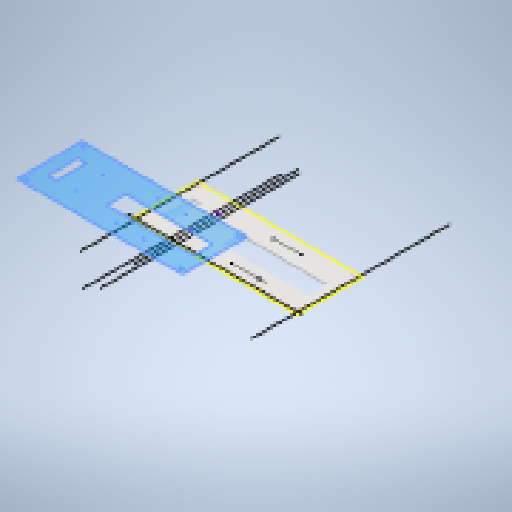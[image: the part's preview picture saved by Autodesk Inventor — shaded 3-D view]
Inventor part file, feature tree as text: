
AUTODESK INVENTOR PART (.ipt)
format: ipt  version: 2024 (Build 280153000, 153)  size: 231,424 bytes
history: native  units: mm
features: extrude x4, sketch x4, other x1
ambient origin geometry x8: Origin, YZ Plane, XZ Plane, XY Plane, X Axis, Y Axis, Z Axis, Center Point
bodies: Body1 (feature_tree)
feature tree (9):
  other  "솔리드1"
  extrude  "돌출1"  Depth=390.0mm
  sketch  "스케치2"
  extrude  "돌출2"  Depth=153.0mm
  extrude  "돌출3"  Depth=3.0mm TaperAngle=0.0deg
  extrude  "돌출5"  Depth=94.0mm
  sketch  "스케치1"
  sketch  "스케치3"
  sketch  "스케치6"
